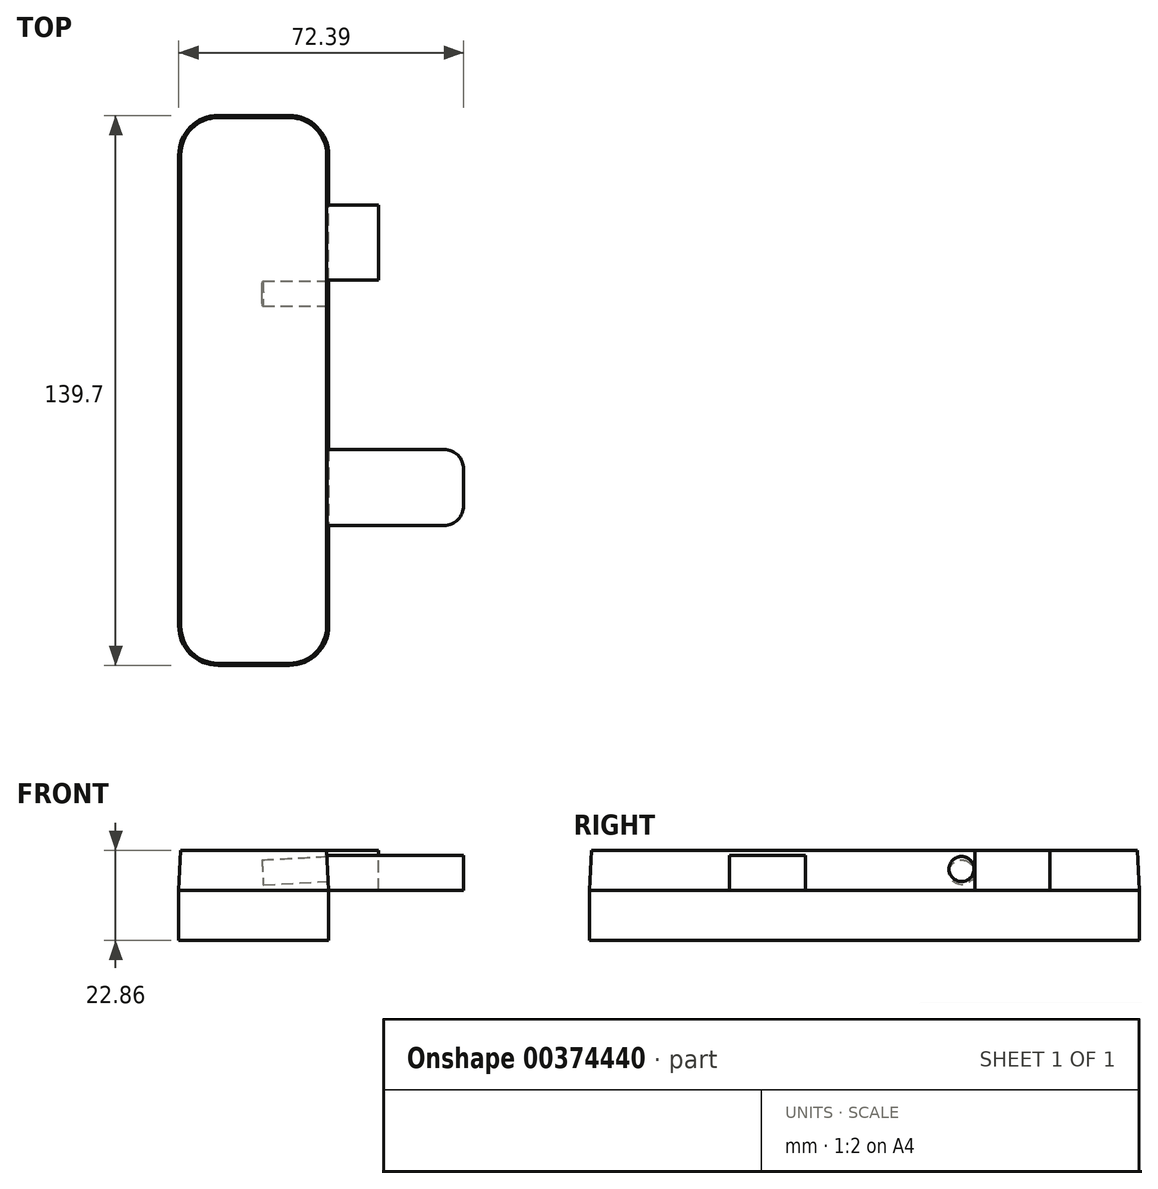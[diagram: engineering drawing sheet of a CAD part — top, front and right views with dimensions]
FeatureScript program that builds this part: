
annotation { "Feature Type Name" : "Feature", "Feature Type Description" : "" }
export const myFeature = defineFeature(function(context is Context, id is Id, definition is map)
    precondition{}
    {
        {
            var Q0;
            Q0=qCreatedBy(makeId("Top.planeOp"),FACE);
            var sketch = newSketch(context, id + "F0", { "sketchPlane" : qUnion([Q0])});
            skLineSegment(sketch, "E0.bottom", {"start": v(-9.05, 69.85) * mm, "end": v(9.05, 69.85) * mm});
            skLineSegment(sketch, "E0.top", {"start": v(-9.05, -69.85) * mm, "end": v(9.05, -69.85) * mm});
            skLineSegment(sketch, "E0.left", {"start": v(-19.05, 59.85) * mm, "end": v(-19.05, -59.85) * mm});
            skLineSegment(sketch, "E0.right", {"start": v(19.05, 59.85) * mm, "end": v(19.05, -59.85) * mm});
            skLineSegment(sketch, "E1", {"start": v(-19.05, 69.85) * mm, "end": v(19.05, -69.85) * mm, "construction": true});
            skPoint(sketch, "E2.visualSharp", {"position": v(-19.05, 69.85) * mm});
            skArc(sketch, "E2.filletArc", {"start": v(-9.05, 69.85) * mm, "mid": v(-16.12, 66.92) * mm, "end": v(-19.05, 59.85) * mm});
            skPoint(sketch, "E3.visualSharp", {"position": v(19.05, 69.85) * mm});
            skArc(sketch, "E3.filletArc", {"start": v(19.05, 59.85) * mm, "mid": v(16.12, 66.92) * mm, "end": v(9.05, 69.85) * mm});
            skPoint(sketch, "E4.visualSharp", {"position": v(19.05, -69.85) * mm});
            skArc(sketch, "E4.filletArc", {"start": v(9.05, -69.85) * mm, "mid": v(16.12, -66.92) * mm, "end": v(19.05, -59.85) * mm});
            skPoint(sketch, "E5.visualSharp", {"position": v(-19.05, -69.85) * mm});
            skArc(sketch, "E5.filletArc", {"start": v(-19.05, -59.85) * mm, "mid": v(-16.12, -66.92) * mm, "end": v(-9.05, -69.85) * mm});
            skSolve(sketch);
        }
        {
            var Q0;
            Q0=makeQuery(id+"F0.imprint","IMPRINT",FACE,{"disambiguationData":[TD([[makeQuery(id+"F0.imprint","IMPRINT",EDGE,{"derivedFrom":sQuery(id+"F0.wireOp",EDGE,"E0.bottom")}),-1.0]])]});
            extrude(context, id + "F1", {"entities" : qUnion([Q0]), "oppositeDirection" : true, "depth" : 12.7 * mm, "hasSecondDirection" : true, "secondDirectionOppositeDirection" : false, "secondDirectionDepth" : 10.16 * mm, "hasSecondDirectionDraft" : true, "secondDirectionDraftAngle" : 3 * degree, "secondDirectionDraftPullDirection" : true});
        }
        {
            var Q0;
            Q0=makeQuery(id+"F1.*.split.splitOp","SPLIT",FACE,{"derivedFrom":makeQuery(id+"F1.opExtrude","SWEPT_FACE",FACE,{"disambiguationData":[OSD([sQuery(id+"F0.wireOp",EDGE,"E0.right")])]})});
            var sketch = newSketch(context, id + "F2", { "sketchPlane" : qUnion([Q0])});
            skLineSegment(sketch, "E6.bottom", {"start": v(-34.3, 0) * mm, "end": v(-14.99, 0) * mm});
            skLineSegment(sketch, "E6.top", {"start": v(-34.3, 8.9) * mm, "end": v(-14.99, 8.9) * mm});
            skLineSegment(sketch, "E6.left", {"start": v(-34.3, 0) * mm, "end": v(-34.3, 8.9) * mm});
            skLineSegment(sketch, "E6.right", {"start": v(-14.99, 0) * mm, "end": v(-14.99, 8.9) * mm});
            skSolve(sketch);
        }
        {
            var Q0;
            Q0 = qSketchRegion(id + "F2", true);
            extrude(context, id + "F3", {"entities" : qUnion([Q0]), "depth" : 34.3 * mm, "hasSecondDirection" : true, "secondDirectionBound" : SecondDirectionBoundingType.UP_TO_NEXT, "secondDirectionOppositeDirection" : true, "secondDirectionDepth" : 25 * mm});
        }
        {
            var Q0;
            Q0=makeQuery(id+"F3.opExtrude","CAP_EDGE",EDGE,{"disambiguationData":[OSD([sQuery(id+"F2.wireOp",EDGE,"E6.left")])],"isStart":false});
            var Q1;
            Q1=makeQuery(id+"F3.opExtrude","CAP_EDGE",EDGE,{"disambiguationData":[OSD([sQuery(id+"F2.wireOp",EDGE,"E6.right")])],"isStart":false});
            fillet(context, id + "F4", {"entities" : qUnion([Q0, Q1]), "radius" : 5 * mm, "tangentPropagation" : true, "allowEdgeOverflow" : false});
        }
        {
            var Q0;
            Q0=makeQuery(id+"F3.opExtrude","CAP_FACE",FACE,{"disambiguationData":[OSD([sQuery(id+"F2.wireOp",EDGE,"E6.bottom"),sQuery(id+"F2.wireOp",EDGE,"E6.top"),sQuery(id+"F2.wireOp",EDGE,"E6.left"),sQuery(id+"F2.wireOp",EDGE,"E6.right")])],"isStart":false});
            var sketch = newSketch(context, id + "F5", { "sketchPlane" : qUnion([Q0])});
            skLineSegment(sketch, "E7", {"start": v(-29.3, 8.9) * mm, "end": v(-19.99, 0) * mm, "construction": true});
            skCircle(sketch, "E8", {"center": v(-24.64, 4.45) * mm, "radius": 3.18 * mm});
            skSolve(sketch);
        }
        {
            var Q0;
            Q0=makeQuery(id+"F5.imprint","IMPRINT",FACE,{"disambiguationData":[TD([[makeQuery(id+"F5.imprint","IMPRINT",EDGE,{"derivedFrom":sQuery(id+"F5.wireOp",EDGE,"E8")}),1.0]])]});
            extrude(context, id + "F6", {"entities" : qUnion([Q0]), "depth" : 25.4 * mm - 8.9 * mm});
        }
        {
            var Q0;
            Q0=makeQuery(id+"F1.*.split.splitOp","SPLIT",FACE,{"derivedFrom":makeQuery(id+"F1.opExtrude","SWEPT_FACE",FACE,{"disambiguationData":[OSD([sQuery(id+"F0.wireOp",EDGE,"E0.right")])]})});
            var sketch = newSketch(context, id + "F7", { "sketchPlane" : qUnion([Q0])});
            skLineSegment(sketch, "E9.bottom", {"start": v(47.15, 0) * mm, "end": v(28.1, 0) * mm});
            skLineSegment(sketch, "E9.top", {"start": v(47.15, 10.16) * mm, "end": v(28.1, 10.16) * mm});
            skLineSegment(sketch, "E9.left", {"start": v(47.15, 0) * mm, "end": v(47.15, 10.16) * mm});
            skLineSegment(sketch, "E9.right", {"start": v(28.1, 0) * mm, "end": v(28.1, 10.16) * mm});
            skSolve(sketch);
        }
        {
            var Q0;
            Q0=makeQuery(id+"F7.imprint","IMPRINT",FACE,{"disambiguationData":[TD([[makeQuery(id+"F7.imprint","IMPRINT",EDGE,{"derivedFrom":sQuery(id+"F7.wireOp",EDGE,"E9.bottom")}),-1.0]])]});
            extrude(context, id + "F8", {"entities" : qUnion([Q0]), "depth" : 12.7 * mm, "hasSecondDirection" : true, "secondDirectionBound" : SecondDirectionBoundingType.UP_TO_NEXT, "secondDirectionOppositeDirection" : true, "secondDirectionDepth" : 25 * mm});
        }
        {
            var Q0;
            Q0=makeQuery(id+"F8.opExtrude","CAP_FACE",FACE,{"disambiguationData":[OSD([sQuery(id+"F7.wireOp",EDGE,"E9.bottom"),sQuery(id+"F7.wireOp",EDGE,"E9.top"),sQuery(id+"F7.wireOp",EDGE,"E9.left"),sQuery(id+"F7.wireOp",EDGE,"E9.right")])],"isStart":false});
            var sketch = newSketch(context, id + "F9", { "sketchPlane" : qUnion([Q0])});
            skLineSegment(sketch, "E10.bottom", {"start": v(44.6, 7) * mm, "end": v(29.6, 7) * mm});
            skLineSegment(sketch, "E10.top", {"start": v(44.6, 2) * mm, "end": v(29.6, 2) * mm});
            skLineSegment(sketch, "E10.left", {"start": v(44.6, 7) * mm, "end": v(44.6, 2) * mm});
            skLineSegment(sketch, "E10.right", {"start": v(29.6, 7) * mm, "end": v(29.6, 2) * mm});
            skSolve(sketch);
        }
        {
            var Q0;
            Q0=makeQuery(id+"F9.imprint","IMPRINT",FACE,{"disambiguationData":[TD([[makeQuery(id+"F9.imprint","IMPRINT",EDGE,{"derivedFrom":sQuery(id+"F9.wireOp",EDGE,"E10.bottom")}),1.0]])]});
            extrude(context, id + "F10", {"entities" : qUnion([Q0]), "operationType" : NewBodyOperationType.ADD, "depth" : 6.35 * mm});
        }
    });
